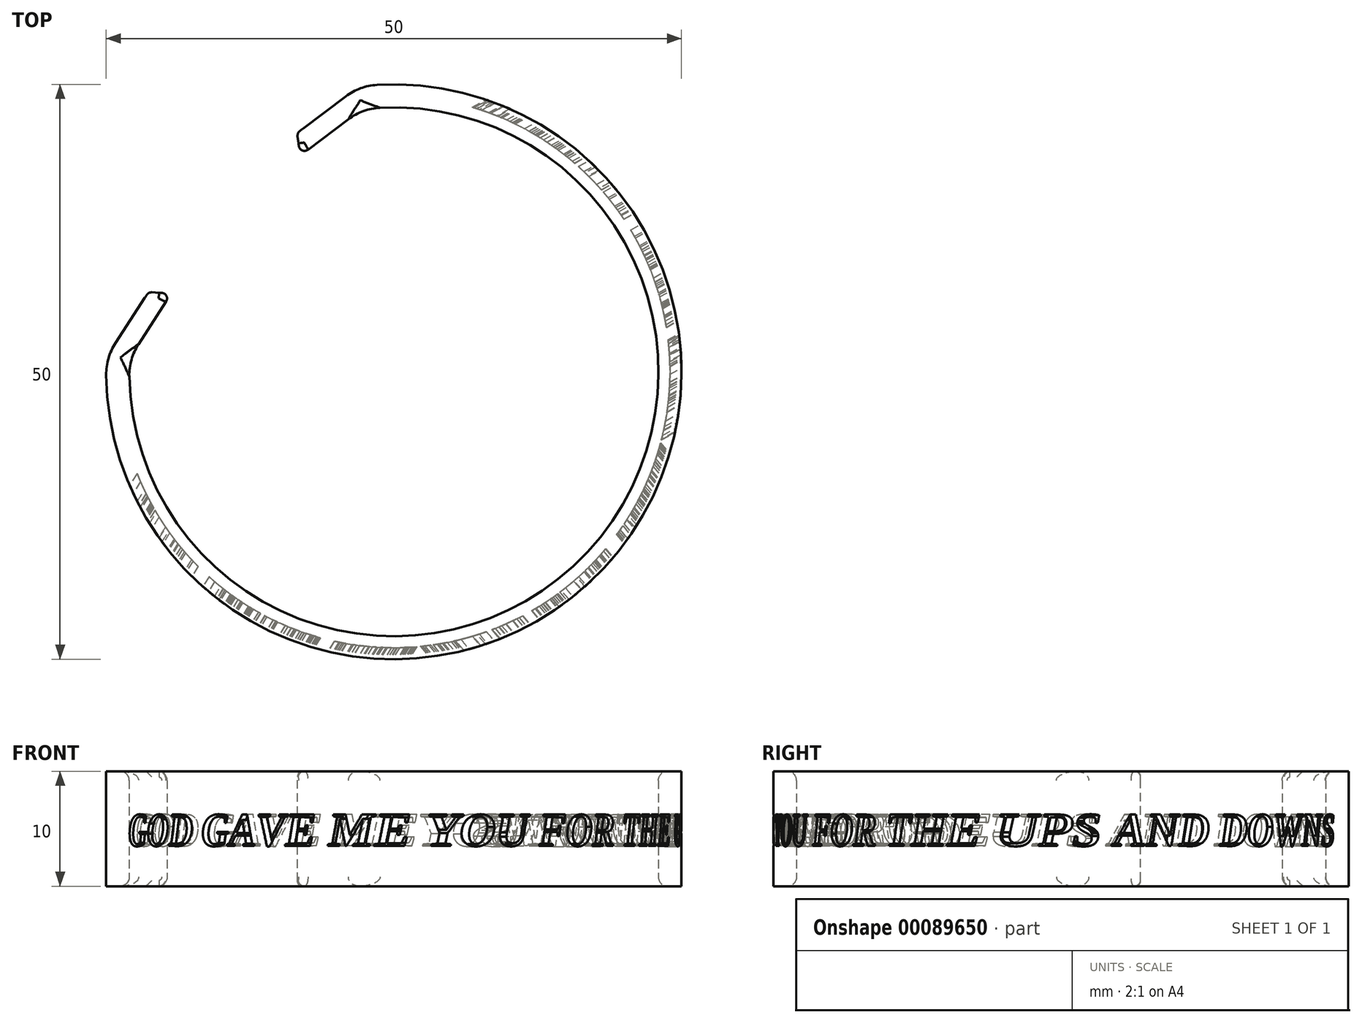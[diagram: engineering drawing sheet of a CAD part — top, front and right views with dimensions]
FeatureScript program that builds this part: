
annotation { "Feature Type Name" : "Feature", "Feature Type Description" : "" }
export const myFeature = defineFeature(function(context is Context, id is Id, definition is map)
    precondition{}
    {
        {
            var Q0;
            Q0=qCreatedBy(makeId("Top.planeOp"),FACE);
            var sketch = newSketch(context, id + "F0", { "sketchPlane" : qUnion([Q0])});
            skCircle(sketch, "E0", {"center": v(0, 0) * mm, "radius": 25 * mm});
            skCircle(sketch, "E1", {"center": v(0, 0) * mm, "radius": 23 * mm});
            skSolve(sketch);
        }
        {
            var Q0;
            Q0=makeQuery(id+"F0.imprint","IMPRINT",FACE,{"disambiguationData":[TD([[makeQuery(id+"F0.imprint","IMPRINT",EDGE,{"derivedFrom":sQuery(id+"F0.wireOp",EDGE,"E0")}),1.0]])]});
            extrude(context, id + "F1", {"entities" : qUnion([Q0]), "depth" : 10 * mm});
        }
        {
            var Q0;
            Q0=qCreatedBy(makeId("Top.planeOp"),FACE);
            var sketch = newSketch(context, id + "F2", { "sketchPlane" : qUnion([Q0])});
            skLineSegment(sketch, "E2", {"start": v(0, 0) * mm, "end": v(-13.25, -21.2) * mm});
            skLineSegment(sketch, "E3", {"start": v(0, 0) * mm, "end": v(16.07, -19.15) * mm});
            skLineSegment(sketch, "E4", {"start": v(0, 0) * mm, "end": v(21.87, 12.12) * mm});
            skLineSegment(sketch, "E5", {"start": v(0, 0) * mm, "end": v(-14, 0) * mm});
            skSolve(sketch);
        }
        {
            var Q0;
            Q0=sQuery(id+"F2.wireOp",EDGE,"E2");
            var Q1;
            Q1=sQuery(id+"F2.wireOp",VERTEX,"E2.end");
            cPlane(context, id + "F3", {"entities" : qUnion([Q0, Q1]), "cplaneType" : CPlaneType.LINE_POINT, "offset" : 25 * mm, "width" : 150 * mm, "height" : 150 * mm});
        }
        {
            var Q0;
            Q0=sQuery(id+"F2.wireOp",VERTEX,"E3.end");
            var Q1;
            Q1=sQuery(id+"F2.wireOp",EDGE,"E3");
            cPlane(context, id + "F4", {"entities" : qUnion([Q0, Q1]), "cplaneType" : CPlaneType.LINE_POINT, "offset" : 10 * mm, "width" : 150 * mm, "height" : 150 * mm});
        }
        {
            var Q0;
            Q0=sQuery(id+"F2.wireOp",VERTEX,"E4.end");
            var Q1;
            Q1=sQuery(id+"F2.wireOp",EDGE,"E4");
            cPlane(context, id + "F5", {"entities" : qUnion([Q0, Q1]), "cplaneType" : CPlaneType.LINE_POINT, "offset" : 150 * mm, "width" : 150 * mm, "height" : 150 * mm});
        }
        {
            var Q0;
            Q0=makeQuery(id+"F1.opExtrude","CAP_FACE",FACE,{"disambiguationData":[OSD([sQuery(id+"F0.wireOp",EDGE,"E0"),sQuery(id+"F0.wireOp",EDGE,"E1")])],"isStart":false});
            var sketch = newSketch(context, id + "F6", { "sketchPlane" : qUnion([Q0])});
            skCircle(sketch, "E6", {"center": v(0, 0) * mm, "radius": 24 * mm});
            skCircle(sketch, "E7", {"center": v(0, 0) * mm, "radius": 23 * mm});
            skSolve(sketch);
        }
        {
            var Q0;
            Q0=qCreatedBy(id+"F3.planeOp",FACE);
            var sketch = newSketch(context, id + "F7", { "sketchPlane" : qUnion([Q0])});
            skPoint(sketch, "E8", {"position": v(0, 5) * mm});
            skLineSegment(sketch, "E9", {"start": v(0, 0) * mm, "end": v(0, 10) * mm, "construction": true});
            skText(sketch, "E10", { "text": "GOD GAVE ME", "fontName": "Tinos-BoldItalic.ttf"});
            const initialGuessF7  = {"E10": [-0.01438, 0.0035, 1, 0, 0.003]};
            skSetInitialGuess(sketch, initialGuessF7);
            skSolve(sketch);
        }
        {
            var Q0;
            Q0=qSketchRegion(id+"F7",true);
            extrude(context, id + "F8", {"entities" : qUnion([Q0]), "operationType" : NewBodyOperationType.REMOVE, "oppositeDirection" : true, "depth" : 25 * mm});
        }
        {
            var Q0;
            Q0=qCreatedBy(id+"F4.planeOp",FACE);
            var sketch = newSketch(context, id + "F9", { "sketchPlane" : qUnion([Q0])});
            skLineSegment(sketch, "E11", {"start": v(0, 0) * mm, "end": v(0, 10) * mm, "construction": true});
            skPoint(sketch, "E12", {"position": v(0, 5) * mm});
            skText(sketch, "E13", { "text": "YOU FOR THE", "fontName": "Tinos-BoldItalic.ttf"});
            const initialGuessF9  = {"E13": [-0.0138, 0.0035, 1, 0, 0.003]};
            skSetInitialGuess(sketch, initialGuessF9);
            skSolve(sketch);
        }
        {
            var Q0;
            Q0=qSketchRegion(id+"F9",true);
            extrude(context, id + "F10", {"entities" : qUnion([Q0]), "operationType" : NewBodyOperationType.REMOVE, "oppositeDirection" : true, "depth" : 25 * mm});
        }
        {
            var Q0;
            Q0=qCreatedBy(id+"F5.planeOp",FACE);
            var sketch = newSketch(context, id + "F11", { "sketchPlane" : qUnion([Q0])});
            skLineSegment(sketch, "E14", {"start": v(0, 0) * mm, "end": v(0, 10) * mm, "construction": true});
            skPoint(sketch, "E15", {"position": v(0, 5) * mm});
            skText(sketch, "E16", { "text": "UPS AND DOWNS", "fontName": "Tinos-BoldItalic.ttf"});
            const initialGuessF11  = {"E16": [-0.01681, 0.0035, 1, 0, 0.003]};
            skSetInitialGuess(sketch, initialGuessF11);
            skSolve(sketch);
        }
        {
            var Q0;
            Q0=qSketchRegion(id+"F11",true);
            extrude(context, id + "F12", {"entities" : qUnion([Q0]), "operationType" : NewBodyOperationType.REMOVE, "oppositeDirection" : true, "depth" : 25 * mm});
        }
        {
            var Q0;
            Q0=qSketchRegion(id+"F6",true);
            var Q1;
            Q1=makeQuery(id+"F1.opExtrude","CAP_FACE",FACE,{"disambiguationData":[OSD([sQuery(id+"F0.wireOp",EDGE,"E0"),sQuery(id+"F0.wireOp",EDGE,"E1")])],"isStart":true});
            extrude(context, id + "F13", {"entities" : qUnion([Q0]), "operationType" : NewBodyOperationType.ADD, "endBound" : BoundingType.UP_TO_SURFACE, "oppositeDirection" : true, "endBoundEntityFace" : qUnion([Q1]), "depth" : 25 * mm});
        }
        {
            var Q0;
            Q0=makeQuery(id+"F1.opExtrude","CAP_FACE",FACE,{"disambiguationData":[OSD([sQuery(id+"F0.wireOp",EDGE,"E0"),sQuery(id+"F0.wireOp",EDGE,"E1")])],"isStart":false});
            var sketch = newSketch(context, id + "F14", { "sketchPlane" : qUnion([Q0])});
            skPoint(sketch, "E17", {"position": v(-7.73, -23.78) * mm});
            skPoint(sketch, "E18", {"position": v(23.18, 9.37) * mm});
            skArc(sketch, "E19", {"start": v(23.18, 9.37) * mm, "mid": v(-18.28, 17.05) * mm, "end": v(-7.73, -23.78) * mm});
            skLineSegment(sketch, "E20", {"start": v(0, 0) * mm, "end": v(23.18, 9.37) * mm});
            skLineSegment(sketch, "E21", {"start": v(0, 0) * mm, "end": v(-7.73, -23.78) * mm});
            skLineSegment(sketch, "E22", {"start": v(0, 0) * mm, "end": v(-7, 0) * mm});
            skLineSegment(sketch, "E23", {"start": v(0, 0) * mm, "end": v(-18.28, 17.05) * mm});
            skLineSegment(sketch, "E24", {"start": v(0, 0) * mm, "end": v(-3.05, 24.81) * mm});
            skLineSegment(sketch, "E25", {"start": v(0, 0) * mm, "end": v(-24.97, 1.3) * mm});
            skSolve(sketch);
        }
        {
            var Q0;
            {var subQ1=sQuery(id+"F14.wireOp",EDGE,"E23");var subQ3=makeQuery(id+"F1.opExtrude","CAP_EDGE",EDGE,{"disambiguationData":[OSD([sQuery(id+"F0.wireOp",EDGE,"E1")])],"isStart":false});var subQ4=makeQuery(id+"F14.imprint","INTERSECT",VERTEX,{"derivedFrom":[subQ3,subQ1]});Q0=makeQuery(id+"F14.imprint","IMPRINT",FACE,{"disambiguationData":[TD([[makeQuery(id+"F14.imprint","IMPRINT",EDGE,{"disambiguationData":[TD([[subQ4,1.0]])],"derivedFrom":subQ3}),1.0]])]});}
            var Q1;
            {var subQ1=sQuery(id+"F14.wireOp",EDGE,"E23");var subQ3=makeQuery(id+"F1.opExtrude","CAP_EDGE",EDGE,{"disambiguationData":[OSD([sQuery(id+"F0.wireOp",EDGE,"E1")])],"isStart":false});var subQ4=makeQuery(id+"F14.imprint","INTERSECT",VERTEX,{"derivedFrom":[subQ3,subQ1]});Q1=makeQuery(id+"F14.imprint","IMPRINT",FACE,{"disambiguationData":[TD([[makeQuery(id+"F14.imprint","IMPRINT",EDGE,{"disambiguationData":[TD([[subQ4,-1.0]])],"derivedFrom":subQ3}),1.0]])]});}
            var Q2;
            {var subQ0=sQuery(id+"F14.wireOp",EDGE,"E23");var subQ1=sQuery(id+"F14.wireOp",EDGE,"E19");var subQ2=makeQuery(id+"F14.imprint","INTERSECT",VERTEX,{"derivedFrom":[subQ1,subQ0]});Q2=makeQuery(id+"F14.imprint","IMPRINT",FACE,{"disambiguationData":[TD([[makeQuery(id+"F14.imprint","IMPRINT",EDGE,{"disambiguationData":[TD([[subQ2,-1.0]])],"derivedFrom":subQ1}),1.0]])]});}
            var Q3;
            {var subQ0=sQuery(id+"F14.wireOp",EDGE,"E23");var subQ1=sQuery(id+"F14.wireOp",EDGE,"E19");var subQ2=makeQuery(id+"F14.imprint","INTERSECT",VERTEX,{"derivedFrom":[subQ1,subQ0]});Q3=makeQuery(id+"F14.imprint","IMPRINT",FACE,{"disambiguationData":[TD([[makeQuery(id+"F14.imprint","IMPRINT",EDGE,{"disambiguationData":[TD([[subQ2,1.0]])],"derivedFrom":subQ1}),1.0]])]});}
            extrude(context, id + "F15", {"entities" : qUnion([Q0, Q1, Q2, Q3]), "operationType" : NewBodyOperationType.REMOVE, "oppositeDirection" : true, "depth" : 25 * mm});
        }
        {
            var Q0;
            Q0=makeQuery(id+"F1.opExtrude","CAP_EDGE",EDGE,{"disambiguationData":[OSD([sQuery(id+"F0.wireOp",EDGE,"E1")])],"isStart":false});
            var Q1;
            Q1=makeQuery(id+"F1.opExtrude","CAP_EDGE",EDGE,{"disambiguationData":[OSD([sQuery(id+"F0.wireOp",EDGE,"E1")])],"isStart":true});
            var Q2;
            {var subQ70=makeQuery(id+"F8.opExtrude","SWEPT_FACE",FACE,{"disambiguationData":[OSD([sQuery(id+"F7.wireOp",EDGE,"af9e3f27-37e7-4adc-a0d5-46bf4d3c87f8.sketch_text.stroke-0")])]});var subQ71=makeQuery(id+"F8.boolean.opBoolean","COPY",FACE,{"derivedFrom":subQ70});var subQ98=sQuery(id+"F0.wireOp",EDGE,"E1");var subQ173=makeQuery(id+"F1.opExtrude","SWEPT_FACE",FACE,{"disambiguationData":[OSD([subQ98])]});var subQ174=makeQuery(id+"F8.boolean.opBoolean","SPLIT",FACE,{"disambiguationData":[TD([subQ70])],"derivedFrom":subQ173});var subQ175=makeQuery(id+"F10.boolean.opBoolean","SPLIT",FACE,{"disambiguationData":[TD([subQ71])],"derivedFrom":subQ174});Q2=makeQuery(id+"FO7dw4kgaFy71Il_1.boolean.opBoolean","INTERSECT",EDGE,{"derivedFrom":[makeQuery(id+"F13.boolean.opBoolean","MERGE",FACE,{"derivedFrom":[makeQuery(id+"F8.boolean.opBoolean","SPLIT",FACE,{"disambiguationData":[TD([makeQuery(id+"F8.opExtrude","SWEPT_FACE",FACE,{"disambiguationData":[OSD([sQuery(id+"F7.wireOp",EDGE,"af9e3f27-37e7-4adc-a0d5-46bf4d3c87f8.sketch_text.stroke-28")])]})])],"derivedFrom":subQ173}),makeQuery(id+"F8.boolean.opBoolean","SPLIT",FACE,{"disambiguationData":[TD([makeQuery(id+"F8.opExtrude","SWEPT_FACE",FACE,{"disambiguationData":[OSD([sQuery(id+"F7.wireOp",EDGE,"af9e3f27-37e7-4adc-a0d5-46bf4d3c87f8.sketch_text.stroke-59")])]})])],"derivedFrom":subQ173}),makeQuery(id+"F10.boolean.opBoolean","SPLIT",FACE,{"disambiguationData":[TD([makeQuery(id+"F10.opExtrude","SWEPT_FACE",FACE,{"disambiguationData":[OSD([sQuery(id+"F9.wireOp",EDGE,"84cfa2e4-d78a-44e2-84a3-9373a785fd08.sketch_text.stroke-20")])]})])],"derivedFrom":subQ174}),makeQuery(id+"F10.boolean.opBoolean","SPLIT",FACE,{"disambiguationData":[TD([makeQuery(id+"F10.opExtrude","SWEPT_FACE",FACE,{"disambiguationData":[OSD([sQuery(id+"F9.wireOp",EDGE,"84cfa2e4-d78a-44e2-84a3-9373a785fd08.sketch_text.stroke-66")])]})])],"derivedFrom":subQ174}),makeQuery(id+"F12.boolean.opBoolean","SPLIT",FACE,{"disambiguationData":[TD([makeQuery(id+"F12.opExtrude","SWEPT_FACE",FACE,{"disambiguationData":[OSD([sQuery(id+"F11.wireOp",EDGE,"b266084a-0614-4de4-91b6-4eca97c6fac9.sketch_text.stroke-68")])]})])],"derivedFrom":subQ175}),makeQuery(id+"F12.boolean.opBoolean","SPLIT",FACE,{"disambiguationData":[TD([subQ71])],"derivedFrom":subQ175}),makeQuery(id+"F13.opExtrude","SWEPT_FACE",FACE,{"disambiguationData":[OSD([sQuery(id+"F6.wireOp",EDGE,"E7")])]})]}),makeQuery(id+"FO7dw4kgaFy71Il_1.opExtrude","SWEPT_FACE",FACE,{"disambiguationData":[OSD([sQuery(id+"F14.wireOp",EDGE,"H89lGICT-0VU6-q7Aq-ubIe-UqfbqTVjVBCE.left")])]})]});}
            var Q3;
            {var subQ70=makeQuery(id+"F8.opExtrude","SWEPT_FACE",FACE,{"disambiguationData":[OSD([sQuery(id+"F7.wireOp",EDGE,"af9e3f27-37e7-4adc-a0d5-46bf4d3c87f8.sketch_text.stroke-0")])]});var subQ71=makeQuery(id+"F8.boolean.opBoolean","COPY",FACE,{"derivedFrom":subQ70});var subQ98=sQuery(id+"F0.wireOp",EDGE,"E1");var subQ173=makeQuery(id+"F1.opExtrude","SWEPT_FACE",FACE,{"disambiguationData":[OSD([subQ98])]});var subQ174=makeQuery(id+"F8.boolean.opBoolean","SPLIT",FACE,{"disambiguationData":[TD([subQ70])],"derivedFrom":subQ173});var subQ175=makeQuery(id+"F10.boolean.opBoolean","SPLIT",FACE,{"disambiguationData":[TD([subQ71])],"derivedFrom":subQ174});Q3=makeQuery(id+"FO7dw4kgaFy71Il_1.boolean.opBoolean","INTERSECT",EDGE,{"derivedFrom":[makeQuery(id+"F13.boolean.opBoolean","MERGE",FACE,{"derivedFrom":[makeQuery(id+"F8.boolean.opBoolean","SPLIT",FACE,{"disambiguationData":[TD([makeQuery(id+"F8.opExtrude","SWEPT_FACE",FACE,{"disambiguationData":[OSD([sQuery(id+"F7.wireOp",EDGE,"af9e3f27-37e7-4adc-a0d5-46bf4d3c87f8.sketch_text.stroke-28")])]})])],"derivedFrom":subQ173}),makeQuery(id+"F8.boolean.opBoolean","SPLIT",FACE,{"disambiguationData":[TD([makeQuery(id+"F8.opExtrude","SWEPT_FACE",FACE,{"disambiguationData":[OSD([sQuery(id+"F7.wireOp",EDGE,"af9e3f27-37e7-4adc-a0d5-46bf4d3c87f8.sketch_text.stroke-59")])]})])],"derivedFrom":subQ173}),makeQuery(id+"F10.boolean.opBoolean","SPLIT",FACE,{"disambiguationData":[TD([makeQuery(id+"F10.opExtrude","SWEPT_FACE",FACE,{"disambiguationData":[OSD([sQuery(id+"F9.wireOp",EDGE,"84cfa2e4-d78a-44e2-84a3-9373a785fd08.sketch_text.stroke-20")])]})])],"derivedFrom":subQ174}),makeQuery(id+"F10.boolean.opBoolean","SPLIT",FACE,{"disambiguationData":[TD([makeQuery(id+"F10.opExtrude","SWEPT_FACE",FACE,{"disambiguationData":[OSD([sQuery(id+"F9.wireOp",EDGE,"84cfa2e4-d78a-44e2-84a3-9373a785fd08.sketch_text.stroke-66")])]})])],"derivedFrom":subQ174}),makeQuery(id+"F12.boolean.opBoolean","SPLIT",FACE,{"disambiguationData":[TD([makeQuery(id+"F12.opExtrude","SWEPT_FACE",FACE,{"disambiguationData":[OSD([sQuery(id+"F11.wireOp",EDGE,"b266084a-0614-4de4-91b6-4eca97c6fac9.sketch_text.stroke-68")])]})])],"derivedFrom":subQ175}),makeQuery(id+"F12.boolean.opBoolean","SPLIT",FACE,{"disambiguationData":[TD([subQ71])],"derivedFrom":subQ175}),makeQuery(id+"F13.opExtrude","SWEPT_FACE",FACE,{"disambiguationData":[OSD([sQuery(id+"F6.wireOp",EDGE,"E7")])]})]}),makeQuery(id+"FO7dw4kgaFy71Il_1.opExtrude","SWEPT_FACE",FACE,{"disambiguationData":[OSD([sQuery(id+"F14.wireOp",EDGE,"H89lGICT-0VU6-q7Aq-ubIe-UqfbqTVjVBCE.bottom")])]})]});}
            fillet(context, id + "F16", {"entities" : qUnion([Q0, Q1, Q2, Q3]), "radius" : 0.8 * mm, "tangentPropagation" : true, "allowEdgeOverflow" : false});
        }
        {
            var Q0;
            Q0=qCreatedBy(makeId("Top.planeOp"),FACE);
            var sketch = newSketch(context, id + "F17", { "sketchPlane" : qUnion([Q0])});
            skLineSegment(sketch, "E26", {"start": v(0, 0) * mm, "end": v(-24.97, 1.3) * mm});
            skLineSegment(sketch, "E27", {"start": v(0, 0) * mm, "end": v(-23.78, 7.73) * mm});
            skLineSegment(sketch, "E28", {"start": v(-24.97, 1.3) * mm, "end": v(-21.32, 6.93) * mm});
            skLineSegment(sketch, "E29", {"start": v(0, 0) * mm, "end": v(-3.05, 24.81) * mm});
            skLineSegment(sketch, "E30", {"start": v(0, 0) * mm, "end": v(-9.37, 23.18) * mm});
            skLineSegment(sketch, "E31", {"start": v(-3.05, 24.81) * mm, "end": v(-8.4, 20.78) * mm});
            skSolve(sketch);
        }
        {
            var Q0;
            Q0=makeQuery(id+"F15.boolean.opBoolean","COPY",FACE,{"derivedFrom":makeQuery(id+"F15.opExtrude","SWEPT_FACE",FACE,{"disambiguationData":[OSD([sQuery(id+"F14.wireOp",EDGE,"E25")])]})});
            var Q1;
            Q1=sQuery(id+"F17.wireOp",EDGE,"E28");
            sweep(context, id + "F18", {"operationType" : NewBodyOperationType.ADD, "profiles" : qUnion([Q0]), "path" : qUnion([Q1])});
        }
        {
            var Q0;
            Q0=makeQuery(id+"F15.boolean.opBoolean","COPY",FACE,{"derivedFrom":makeQuery(id+"F15.opExtrude","SWEPT_FACE",FACE,{"disambiguationData":[OSD([sQuery(id+"F14.wireOp",EDGE,"E24")])]})});
            var Q1;
            Q1=sQuery(id+"F17.wireOp",EDGE,"E31");
            sweep(context, id + "F19", {"operationType" : NewBodyOperationType.ADD, "profiles" : qUnion([Q0]), "path" : qUnion([Q1])});
        }
        {
            var Q0;
            Q0=makeQuery(id+"F18.opSweep","CAP_EDGE",EDGE,{"disambiguationData":[OSD([sQuery(id+"F0.wireOp",EDGE,"E1"),sQuery(id+"F6.wireOp",EDGE,"E7"),sQuery(id+"F14.wireOp",EDGE,"E25"),sQuery(id+"F17.wireOp",VERTEX,"169d4d21-90c5-4424-b8fc-225aa61ef7c7.end")])],"isStart":false});
            var Q1;
            Q1=makeQuery(id+"F18.opSweep","CAP_EDGE",EDGE,{"disambiguationData":[OSD([sQuery(id+"F14.wireOp",EDGE,"E19"),sQuery(id+"F14.wireOp",EDGE,"E25"),sQuery(id+"F17.wireOp",VERTEX,"169d4d21-90c5-4424-b8fc-225aa61ef7c7.end")])],"isStart":false});
            var Q2;
            Q2=makeQuery(id+"F19.opSweep","CAP_EDGE",EDGE,{"disambiguationData":[OSD([sQuery(id+"F14.wireOp",EDGE,"E19"),sQuery(id+"F14.wireOp",EDGE,"E24"),sQuery(id+"F17.wireOp",VERTEX,"U52S8eCT-Fjog-FokC-R4AH-etOpDHYjb7Mq.end")])],"isStart":false});
            var Q3;
            Q3=makeQuery(id+"F19.opSweep","CAP_EDGE",EDGE,{"disambiguationData":[OSD([sQuery(id+"F0.wireOp",EDGE,"E1"),sQuery(id+"F6.wireOp",EDGE,"E7"),sQuery(id+"F14.wireOp",EDGE,"E24"),sQuery(id+"F17.wireOp",VERTEX,"U52S8eCT-Fjog-FokC-R4AH-etOpDHYjb7Mq.end")])],"isStart":false});
            fillet(context, id + "F20", {"entities" : qUnion([Q0, Q1, Q2, Q3]), "radius" : 0.5 * mm, "tangentPropagation" : true, "allowEdgeOverflow" : false});
        }
        {
            var Q0;
            {var subQ0=sQuery(id+"F14.wireOp",EDGE,"E25");var subQ1=sQuery(id+"F14.wireOp",EDGE,"E19");Q0=makeQuery(id+"F18.boolean.opBoolean","MERGE",EDGE,{"derivedFrom":[makeQuery(id+"F15.boolean.opBoolean","COPY",EDGE,{"derivedFrom":makeQuery(id+"F15.opExtrude","SWEPT_EDGE",EDGE,{"disambiguationData":[OSD([subQ1,subQ0])]})}),makeQuery(id+"F18.opSweep","CAP_EDGE",EDGE,{"disambiguationData":[OSD([subQ1,subQ0,sQuery(id+"F17.wireOp",VERTEX,"E28.start")])],"isStart":true})]});}
            var Q1;
            {var subQ0=sQuery(id+"F14.wireOp",EDGE,"E24");var subQ1=sQuery(id+"F14.wireOp",EDGE,"E19");Q1=makeQuery(id+"F19.boolean.opBoolean","MERGE",EDGE,{"derivedFrom":[makeQuery(id+"F15.boolean.opBoolean","COPY",EDGE,{"derivedFrom":makeQuery(id+"F15.opExtrude","SWEPT_EDGE",EDGE,{"disambiguationData":[OSD([subQ1,subQ0])]})}),makeQuery(id+"F19.opSweep","CAP_EDGE",EDGE,{"disambiguationData":[OSD([subQ1,subQ0,sQuery(id+"F17.wireOp",VERTEX,"U52S8eCT-Fjog-FokC-R4AH-etOpDHYjb7Mq.start")])],"isStart":true})]});}
            var Q2;
            {var subQ0=sQuery(id+"F14.wireOp",EDGE,"E25");var subQ1=sQuery(id+"F6.wireOp",EDGE,"E7");var subQ2=sQuery(id+"F0.wireOp",EDGE,"E1");var subQ476=makeQuery(id+"F8.opExtrude","SWEPT_FACE",FACE,{"disambiguationData":[OSD([sQuery(id+"F7.wireOp",EDGE,"E10.sketch_text.stroke-0")])]});var subQ477=makeQuery(id+"F8.boolean.opBoolean","COPY",FACE,{"derivedFrom":subQ476});var subQ500=makeQuery(id+"F10.opExtrude","SWEPT_FACE",FACE,{"disambiguationData":[OSD([sQuery(id+"F9.wireOp",EDGE,"E13.sketch_text.stroke-193")])]});var subQ505=makeQuery(id+"F10.opExtrude","SWEPT_FACE",FACE,{"disambiguationData":[OSD([sQuery(id+"F9.wireOp",EDGE,"E13.sketch_text.stroke-202")])]});var subQ513=makeQuery(id+"F8.opExtrude","SWEPT_FACE",FACE,{"disambiguationData":[OSD([sQuery(id+"F7.wireOp",EDGE,"E10.sketch_text.stroke-182")])]});var subQ523=makeQuery(id+"F1.opExtrude","SWEPT_FACE",FACE,{"disambiguationData":[OSD([subQ2])]});var subQ524=makeQuery(id+"F8.boolean.opBoolean","SPLIT",FACE,{"disambiguationData":[TD([subQ476])],"derivedFrom":subQ523});var subQ525=makeQuery(id+"F10.boolean.opBoolean","SPLIT",FACE,{"disambiguationData":[TD([subQ477])],"derivedFrom":subQ524});Q2=makeQuery(id+"F18.boolean.opBoolean","MERGE",EDGE,{"derivedFrom":[makeQuery(id+"F15.boolean.opBoolean","INTERSECT",EDGE,{"derivedFrom":[makeQuery(id+"F13.boolean.opBoolean","MERGE",FACE,{"derivedFrom":[makeQuery(id+"F8.boolean.opBoolean","SPLIT",FACE,{"disambiguationData":[TD([makeQuery(id+"F8.opExtrude","SWEPT_FACE",FACE,{"disambiguationData":[OSD([sQuery(id+"F7.wireOp",EDGE,"E10.sketch_text.stroke-107")])]})])],"derivedFrom":subQ523}),makeQuery(id+"F8.boolean.opBoolean","SPLIT",FACE,{"disambiguationData":[TD([makeQuery(id+"F8.opExtrude","SWEPT_FACE",FACE,{"disambiguationData":[OSD([sQuery(id+"F7.wireOp",EDGE,"E10.sketch_text.stroke-47")])]})])],"derivedFrom":subQ523}),makeQuery(id+"F8.boolean.opBoolean","SPLIT",FACE,{"disambiguationData":[TD([makeQuery(id+"F8.opExtrude","SWEPT_FACE",FACE,{"disambiguationData":[OSD([sQuery(id+"F7.wireOp",EDGE,"E10.sketch_text.stroke-25")])]})])],"derivedFrom":subQ523}),makeQuery(id+"F10.boolean.opBoolean","SPLIT",FACE,{"disambiguationData":[TD([makeQuery(id+"F8.boolean.opBoolean","COPY",FACE,{"derivedFrom":subQ513})])],"derivedFrom":subQ524}),makeQuery(id+"F10.boolean.opBoolean","SPLIT",FACE,{"disambiguationData":[TD([makeQuery(id+"F10.opExtrude","SWEPT_FACE",FACE,{"disambiguationData":[OSD([sQuery(id+"F9.wireOp",EDGE,"E13.sketch_text.stroke-132")])]})])],"derivedFrom":subQ524}),makeQuery(id+"F10.boolean.opBoolean","SPLIT",FACE,{"disambiguationData":[TD([makeQuery(id+"F10.opExtrude","SWEPT_FACE",FACE,{"disambiguationData":[OSD([sQuery(id+"F9.wireOp",EDGE,"E13.sketch_text.stroke-21")])]})])],"derivedFrom":subQ524}),makeQuery(id+"F10.boolean.opBoolean","SPLIT",FACE,{"disambiguationData":[TD([makeQuery(id+"F10.opExtrude","SWEPT_FACE",FACE,{"disambiguationData":[OSD([sQuery(id+"F9.wireOp",EDGE,"E13.sketch_text.stroke-90")])]})])],"derivedFrom":subQ524}),makeQuery(id+"F12.boolean.opBoolean","SPLIT",FACE,{"disambiguationData":[TD([makeQuery(id+"F10.boolean.opBoolean","COPY",FACE,{"derivedFrom":subQ500})])],"derivedFrom":subQ525}),makeQuery(id+"F12.boolean.opBoolean","SPLIT",FACE,{"disambiguationData":[TD([makeQuery(id+"F12.opExtrude","SWEPT_FACE",FACE,{"disambiguationData":[OSD([sQuery(id+"F11.wireOp",EDGE,"E16.sketch_text.stroke-94")])]})])],"derivedFrom":subQ525}),makeQuery(id+"F12.boolean.opBoolean","SPLIT",FACE,{"disambiguationData":[TD([makeQuery(id+"F10.boolean.opBoolean","COPY",FACE,{"derivedFrom":subQ505})])],"derivedFrom":subQ525}),makeQuery(id+"F12.boolean.opBoolean","SPLIT",FACE,{"disambiguationData":[TD([makeQuery(id+"F12.opExtrude","SWEPT_FACE",FACE,{"disambiguationData":[OSD([sQuery(id+"F11.wireOp",EDGE,"E16.sketch_text.stroke-117")])]})])],"derivedFrom":subQ525}),makeQuery(id+"F12.boolean.opBoolean","SPLIT",FACE,{"disambiguationData":[TD([makeQuery(id+"F12.opExtrude","SWEPT_FACE",FACE,{"disambiguationData":[OSD([sQuery(id+"F11.wireOp",EDGE,"E16.sketch_text.stroke-136")])]})])],"derivedFrom":subQ525}),makeQuery(id+"F12.boolean.opBoolean","SPLIT",FACE,{"disambiguationData":[TD([makeQuery(id+"F12.opExtrude","SWEPT_FACE",FACE,{"disambiguationData":[OSD([sQuery(id+"F11.wireOp",EDGE,"E16.sketch_text.stroke-23")])]})])],"derivedFrom":subQ525}),makeQuery(id+"F12.boolean.opBoolean","SPLIT",FACE,{"disambiguationData":[TD([makeQuery(id+"F12.opExtrude","SWEPT_FACE",FACE,{"disambiguationData":[OSD([sQuery(id+"F11.wireOp",EDGE,"E16.sketch_text.stroke-155")])]})])],"derivedFrom":subQ525}),makeQuery(id+"F12.boolean.opBoolean","SPLIT",FACE,{"disambiguationData":[TD([subQ477])],"derivedFrom":subQ525}),makeQuery(id+"F13.opExtrude","SWEPT_FACE",FACE,{"disambiguationData":[OSD([subQ1])]})]}),makeQuery(id+"F15.opExtrude","SWEPT_FACE",FACE,{"disambiguationData":[OSD([subQ0])]})]}),makeQuery(id+"F18.opSweep","CAP_EDGE",EDGE,{"disambiguationData":[OSD([subQ2,subQ1,subQ0,sQuery(id+"F17.wireOp",VERTEX,"E28.start")])],"isStart":true})]});}
            var Q3;
            {var subQ0=sQuery(id+"F14.wireOp",EDGE,"E24");var subQ1=sQuery(id+"F6.wireOp",EDGE,"E7");var subQ2=sQuery(id+"F0.wireOp",EDGE,"E1");var subQ476=makeQuery(id+"F8.opExtrude","SWEPT_FACE",FACE,{"disambiguationData":[OSD([sQuery(id+"F7.wireOp",EDGE,"E10.sketch_text.stroke-0")])]});var subQ477=makeQuery(id+"F8.boolean.opBoolean","COPY",FACE,{"derivedFrom":subQ476});var subQ500=makeQuery(id+"F10.opExtrude","SWEPT_FACE",FACE,{"disambiguationData":[OSD([sQuery(id+"F9.wireOp",EDGE,"E13.sketch_text.stroke-193")])]});var subQ505=makeQuery(id+"F10.opExtrude","SWEPT_FACE",FACE,{"disambiguationData":[OSD([sQuery(id+"F9.wireOp",EDGE,"E13.sketch_text.stroke-202")])]});var subQ513=makeQuery(id+"F8.opExtrude","SWEPT_FACE",FACE,{"disambiguationData":[OSD([sQuery(id+"F7.wireOp",EDGE,"E10.sketch_text.stroke-182")])]});var subQ523=makeQuery(id+"F1.opExtrude","SWEPT_FACE",FACE,{"disambiguationData":[OSD([subQ2])]});var subQ524=makeQuery(id+"F8.boolean.opBoolean","SPLIT",FACE,{"disambiguationData":[TD([subQ476])],"derivedFrom":subQ523});var subQ525=makeQuery(id+"F10.boolean.opBoolean","SPLIT",FACE,{"disambiguationData":[TD([subQ477])],"derivedFrom":subQ524});Q3=makeQuery(id+"F19.boolean.opBoolean","MERGE",EDGE,{"derivedFrom":[makeQuery(id+"F15.boolean.opBoolean","INTERSECT",EDGE,{"derivedFrom":[makeQuery(id+"F13.boolean.opBoolean","MERGE",FACE,{"derivedFrom":[makeQuery(id+"F8.boolean.opBoolean","SPLIT",FACE,{"disambiguationData":[TD([makeQuery(id+"F8.opExtrude","SWEPT_FACE",FACE,{"disambiguationData":[OSD([sQuery(id+"F7.wireOp",EDGE,"E10.sketch_text.stroke-107")])]})])],"derivedFrom":subQ523}),makeQuery(id+"F8.boolean.opBoolean","SPLIT",FACE,{"disambiguationData":[TD([makeQuery(id+"F8.opExtrude","SWEPT_FACE",FACE,{"disambiguationData":[OSD([sQuery(id+"F7.wireOp",EDGE,"E10.sketch_text.stroke-47")])]})])],"derivedFrom":subQ523}),makeQuery(id+"F8.boolean.opBoolean","SPLIT",FACE,{"disambiguationData":[TD([makeQuery(id+"F8.opExtrude","SWEPT_FACE",FACE,{"disambiguationData":[OSD([sQuery(id+"F7.wireOp",EDGE,"E10.sketch_text.stroke-25")])]})])],"derivedFrom":subQ523}),makeQuery(id+"F10.boolean.opBoolean","SPLIT",FACE,{"disambiguationData":[TD([makeQuery(id+"F8.boolean.opBoolean","COPY",FACE,{"derivedFrom":subQ513})])],"derivedFrom":subQ524}),makeQuery(id+"F10.boolean.opBoolean","SPLIT",FACE,{"disambiguationData":[TD([makeQuery(id+"F10.opExtrude","SWEPT_FACE",FACE,{"disambiguationData":[OSD([sQuery(id+"F9.wireOp",EDGE,"E13.sketch_text.stroke-132")])]})])],"derivedFrom":subQ524}),makeQuery(id+"F10.boolean.opBoolean","SPLIT",FACE,{"disambiguationData":[TD([makeQuery(id+"F10.opExtrude","SWEPT_FACE",FACE,{"disambiguationData":[OSD([sQuery(id+"F9.wireOp",EDGE,"E13.sketch_text.stroke-21")])]})])],"derivedFrom":subQ524}),makeQuery(id+"F10.boolean.opBoolean","SPLIT",FACE,{"disambiguationData":[TD([makeQuery(id+"F10.opExtrude","SWEPT_FACE",FACE,{"disambiguationData":[OSD([sQuery(id+"F9.wireOp",EDGE,"E13.sketch_text.stroke-90")])]})])],"derivedFrom":subQ524}),makeQuery(id+"F12.boolean.opBoolean","SPLIT",FACE,{"disambiguationData":[TD([makeQuery(id+"F10.boolean.opBoolean","COPY",FACE,{"derivedFrom":subQ500})])],"derivedFrom":subQ525}),makeQuery(id+"F12.boolean.opBoolean","SPLIT",FACE,{"disambiguationData":[TD([makeQuery(id+"F12.opExtrude","SWEPT_FACE",FACE,{"disambiguationData":[OSD([sQuery(id+"F11.wireOp",EDGE,"E16.sketch_text.stroke-94")])]})])],"derivedFrom":subQ525}),makeQuery(id+"F12.boolean.opBoolean","SPLIT",FACE,{"disambiguationData":[TD([makeQuery(id+"F10.boolean.opBoolean","COPY",FACE,{"derivedFrom":subQ505})])],"derivedFrom":subQ525}),makeQuery(id+"F12.boolean.opBoolean","SPLIT",FACE,{"disambiguationData":[TD([makeQuery(id+"F12.opExtrude","SWEPT_FACE",FACE,{"disambiguationData":[OSD([sQuery(id+"F11.wireOp",EDGE,"E16.sketch_text.stroke-117")])]})])],"derivedFrom":subQ525}),makeQuery(id+"F12.boolean.opBoolean","SPLIT",FACE,{"disambiguationData":[TD([makeQuery(id+"F12.opExtrude","SWEPT_FACE",FACE,{"disambiguationData":[OSD([sQuery(id+"F11.wireOp",EDGE,"E16.sketch_text.stroke-136")])]})])],"derivedFrom":subQ525}),makeQuery(id+"F12.boolean.opBoolean","SPLIT",FACE,{"disambiguationData":[TD([makeQuery(id+"F12.opExtrude","SWEPT_FACE",FACE,{"disambiguationData":[OSD([sQuery(id+"F11.wireOp",EDGE,"E16.sketch_text.stroke-23")])]})])],"derivedFrom":subQ525}),makeQuery(id+"F12.boolean.opBoolean","SPLIT",FACE,{"disambiguationData":[TD([makeQuery(id+"F12.opExtrude","SWEPT_FACE",FACE,{"disambiguationData":[OSD([sQuery(id+"F11.wireOp",EDGE,"E16.sketch_text.stroke-155")])]})])],"derivedFrom":subQ525}),makeQuery(id+"F12.boolean.opBoolean","SPLIT",FACE,{"disambiguationData":[TD([subQ477])],"derivedFrom":subQ525}),makeQuery(id+"F13.opExtrude","SWEPT_FACE",FACE,{"disambiguationData":[OSD([subQ1])]})]}),makeQuery(id+"F15.opExtrude","SWEPT_FACE",FACE,{"disambiguationData":[OSD([subQ0])]})]}),makeQuery(id+"F19.opSweep","CAP_EDGE",EDGE,{"disambiguationData":[OSD([subQ2,subQ1,subQ0,sQuery(id+"F17.wireOp",VERTEX,"E31.start")])],"isStart":true})]});}
            fillet(context, id + "F21", {"entities" : qUnion([Q0, Q1, Q2, Q3]), "radius" : 5 * mm, "tangentPropagation" : true, "allowEdgeOverflow" : false});
        }
    });
